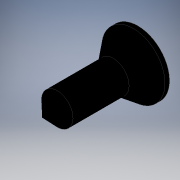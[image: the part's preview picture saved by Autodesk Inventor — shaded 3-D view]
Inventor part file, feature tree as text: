
AUTODESK INVENTOR PART (.ipt)
format: ipt  version: 2019 (Build 230136000, 136)  size: 134,144 bytes
history: native  units: mm
features: other x7, sketch x2, revolve x1, extrude x1
ambient origin geometry x8: Origin, YZ Plane, XZ Plane, XY Plane, X Axis, Y Axis, Z Axis, Center Point
bodies: Solid1 (feature_tree)
feature tree (11):
  revolve  "Revolution1"  [1 undecoded]
  extrude  "Extrusion1"  [1 undecoded]
  other  "CS_ANBAU_XY"
  other  "CS_ANBAU_YZ"
  other  "CS_ANBAU_ZX"
  other  "CS_ANBAU_X"
  other  "CS_ANBAU_Y"
  other  "CS_ANBAU_Z"
  other  "CS_ANBAU_Center"
  sketch  "Sketch_1"  dims[d0=360.0deg d1=2.0mm d2=0.0mm]
  sketch  "Sketch_3"  dims[d3=0.0mm]
note: 2 required parameter values undecoded (feature->parameter linkage not recoverable at this tier; creation-order binding heuristic only, values carry confidence <= 0.55)